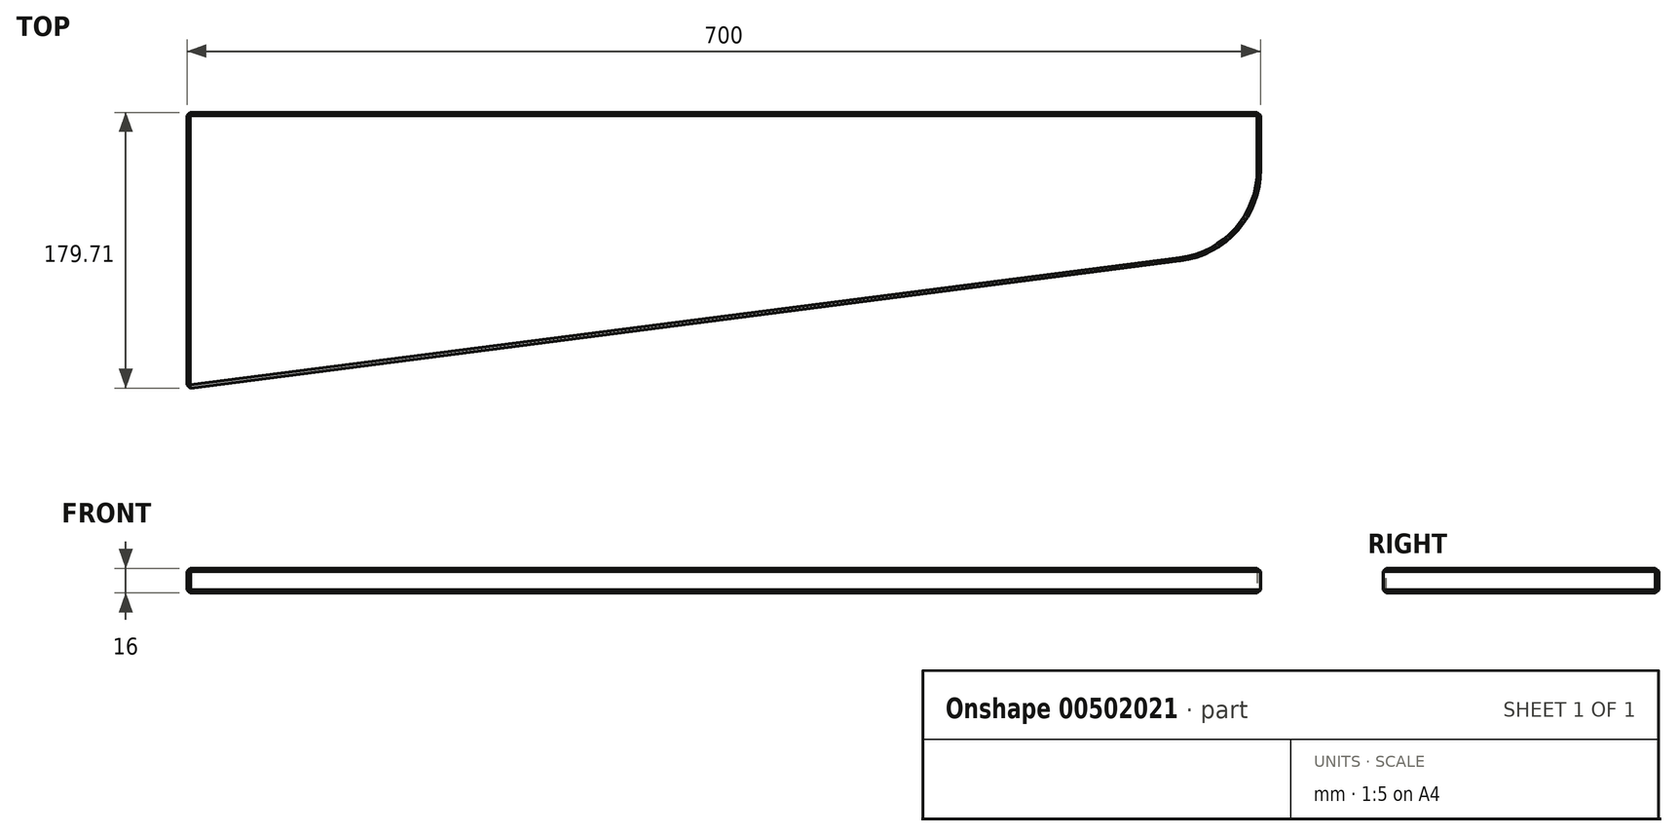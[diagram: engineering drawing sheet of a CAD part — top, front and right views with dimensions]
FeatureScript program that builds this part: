
annotation { "Feature Type Name" : "Feature", "Feature Type Description" : "" }
export const myFeature = defineFeature(function(context is Context, id is Id, definition is map)
    precondition{}
    {
        {
            var Q0;
            Q0=qCreatedBy(makeId("Top.planeOp"),FACE);
            var sketch = newSketch(context, id + "F0", { "sketchPlane" : qUnion([Q0])});
            skLineSegment(sketch, "E0", {"start": v(0, 0) * mm, "end": v(0, 180) * mm});
            skLineSegment(sketch, "E1", {"start": v(0, 180) * mm, "end": v(700, 180) * mm});
            skLineSegment(sketch, "E2", {"start": v(700, 180) * mm, "end": v(700, 90) * mm});
            skLineSegment(sketch, "E3", {"start": v(700, 90) * mm, "end": v(0, 0) * mm});
            skSolve(sketch);
        }
        {
            var Q0;
            Q0 = qSketchRegion(id + "F0", true);
            extrude(context, id + "F1", {"entities" : qUnion([Q0]), "depth" : 16 * mm, "offsetDistance" : 25 * mm});
        }
        {
            var Q0;
            Q0=makeQuery(id+"F1.opExtrude","SWEPT_EDGE",EDGE,{"disambiguationData":[OSD([sQuery(id+"F0.wireOp",EDGE,"E2"),sQuery(id+"F0.wireOp",EDGE,"E3")])]});
            fillet(context, id + "F2", {"entities" : qUnion([Q0]), "radius" : 60 * mm, "tangentPropagation" : true, "allowEdgeOverflow" : false});
        }
        {
            var Q0;
            Q0=makeQuery(id+"F1.opExtrude","CAP_EDGE",EDGE,{"disambiguationData":[OSD([sQuery(id+"F0.wireOp",EDGE,"E3")])],"isStart":false});
            var Q1;
            Q1=makeQuery(id+"F1.opExtrude","CAP_EDGE",EDGE,{"disambiguationData":[OSD([sQuery(id+"F0.wireOp",EDGE,"E1")])],"isStart":false});
            var Q2;
            Q2=makeQuery(id+"F1.opExtrude","CAP_EDGE",EDGE,{"disambiguationData":[OSD([sQuery(id+"F0.wireOp",EDGE,"E0")])],"isStart":false});
            var Q3;
            Q3=makeQuery(id+"F1.opExtrude","SWEPT_EDGE",EDGE,{"disambiguationData":[OSD([sQuery(id+"F0.wireOp",EDGE,"E0"),sQuery(id+"F0.wireOp",EDGE,"E3")])]});
            var Q4;
            Q4=makeQuery(id+"F1.opExtrude","SWEPT_EDGE",EDGE,{"disambiguationData":[OSD([sQuery(id+"F0.wireOp",EDGE,"E1"),sQuery(id+"F0.wireOp",EDGE,"E2")])]});
            var Q5;
            Q5=makeQuery(id+"F1.opExtrude","CAP_EDGE",EDGE,{"disambiguationData":[OSD([sQuery(id+"F0.wireOp",EDGE,"E2")])],"isStart":true});
            var Q6;
            Q6=makeQuery(id+"F1.opExtrude","CAP_EDGE",EDGE,{"disambiguationData":[OSD([sQuery(id+"F0.wireOp",EDGE,"E1")])],"isStart":true});
            var Q7;
            Q7=makeQuery(id+"F1.opExtrude","SWEPT_EDGE",EDGE,{"disambiguationData":[OSD([sQuery(id+"F0.wireOp",EDGE,"E0"),sQuery(id+"F0.wireOp",EDGE,"E1")])]});
            var Q8;
            Q8=makeQuery(id+"F1.opExtrude","CAP_EDGE",EDGE,{"disambiguationData":[OSD([sQuery(id+"F0.wireOp",EDGE,"E0")])],"isStart":true});
            chamfer(context, id + "F3", {"entities" : qUnion([Q0, Q1, Q2, Q3, Q4, Q5, Q6, Q7, Q8]), "width" : 2 * mm, "tangentPropagation" : true});
        }
    });
